# Revit family: ASafe_ASafeHQLtd_HndrlSym_eFlexPedestrianBarrier3Rail
name_source: partatom
category: Railings
revit_build: Autodesk Revit 2018 (Build: 20170630_0700(x64)
units: mm (PartAtom-declared; Revit-internal decimal feet)

## family parameters
Always vertical = Yes
Cut with Voids When Loaded = No
Shared = No
Work Plane-Based = Yes

## types (3) — shared parameters
AssetType = Fixed
BasePlateSize = 180 x 180 mm
Category = Ss_25_15_60_35:Handrail systems
ChemicalResistance = Excellent - ISO/TR 10358
Color = Signal yellow
Constituents = Caps and fixings
Default Elevation = 1219 mm
Deflection = 230 mm at maximum energy
DoubleAngledEndPost = No
DurationUnit = year
Duty = Light
FlashPoint = 350°C to 370°C
HandrailHeight = 1050 mm
HasHygieneSeals = No
Height = 1181 mm
IfcExportAs = IfcRailingType
IfcExportType = USERDEFINED
IgnitionTemperature = 370°C to 390°C
ImpactJoules = Static Load tested to 2 kN
ImpactZone = 233-1100 mm
IsExternal = Yes
LiftingForce = 1 kN
ManufacturerName = A-Safe (HQ) Ltd
ManufacturerURL = https://www.asafe.com
Material = Memaplex
ModelReference = eFlex™ Pedestrian Barrier 3 Rail
MountingType = Floor fixed
NBSCertification = www.nationalbimlibrary.com/cert/dev54ljc
NBSDescription = Handrail system
NBSReference = 25-25-10/135
NominalHeight = 1181 mm
NominalWidth = 130 mm
PostHeight = 1181 mm
ProductInformation = https://www.asafe.com
StaticRating = 1015-1016 Ω
Status = UNSET
TemperatureRange = -10°C to 50°C
Toxicity = Not hazardous
Uniclass2015Code = Ss_25_15_60_35
Uniclass2015Title = Handrail systems
Uniclass2015Version = Systems v1.10
Version = 1
WarrantyDurationUnit = year
zero-valued in all types: Diameter

## per-type parameters (varying)
| type | AngledEndPost | BIMObjectName | EndPostAngle | Name | PostAngle |
| End | No | ASafe_ASafeHQLtd_HandrailSystem_eFlexPedestrianBarrier3Rail_End | 90.00° | HandrailSystem_eFlexPedestrianBarrier3Rail_End_ASafeHQLtd |  |
| 90Degrees | Yes | ASafe_ASafeHQLtd_HandrailSystem_eFlexPedestrianBarrier3Rail_90Degrees | 90.00° | HandrailSystem_eFlexPedestrianBarrier3Rail_90Degrees_ASafeHQLtd | 90° |
| Mid | Yes | ASafe_ASafeHQLtd_HandrailSystem_eFlexPedestrianBarrier3Rail_Mid | 180.00° | HandrailSystem_eFlexPedestrianBarrier3Rail_Mid_ASafeHQLtd | 180° |

## geometry (parser evidence)
native form markers: Extrusion x1, Sweep x10
no freeform markers — native parametric forms only
